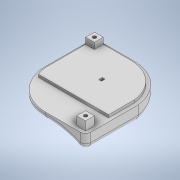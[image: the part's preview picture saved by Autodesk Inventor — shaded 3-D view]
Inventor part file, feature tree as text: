
AUTODESK INVENTOR PART (.ipt)
format: ipt  version: 2020 (Build 240168000, 168)  size: 255,488 bytes
history: native  units: mm
features: other x4, sketch x3, extrude x2, fillet x2, plane x1, hole x1, projected_geometry x1
ambient origin geometry x8: Origin, YZ Plane, XZ Plane, XY Plane, X Axis, Y Axis, Z Axis, Center Point
bodies: Body1 (feature_tree)
feature tree (14):
  other  "modelo2bateria.ipt"
  extrude  "Extrusión1"  Depth=10.0mm
  fillet  "Empalme1"  Radius=1.95mm
  fillet  "Empalme2"  Radius=10.0mm
  extrude  "Extrusión2"  Depth=3.0mm
  plane  "Plano de trabajo1"
  hole  "Agujero1"  [1 undecoded]
  other  "Sólido2::modelo2bateria.ipt"
  other  "OperaciónIdentificador1"
  sketch  "Boceto1"  dims[d0=10.0mm d1=1.5mm d2=1.95mm d3=10.0mm d4=0.0mm]
  sketch  "Boceto2"  dims[d5=3.0mm d6=3.0mm]
  projected_geometry  "Contorno proyectado1"
  sketch  "Boceto3"  dims[d7=5.0mm d8=5.0mm d9=3.5mm d10=0.0mm d11=-13.5mm d12=1.94056mm d13=15.029mm d14=4.0mm d15=2.0mm d16=90.0deg d17=8.0mm d18=0.0mm]
  other  "Sólido1"
note: 1 required parameter value undecoded (feature->parameter linkage not recoverable at this tier; creation-order binding heuristic only, values carry confidence <= 0.55)
